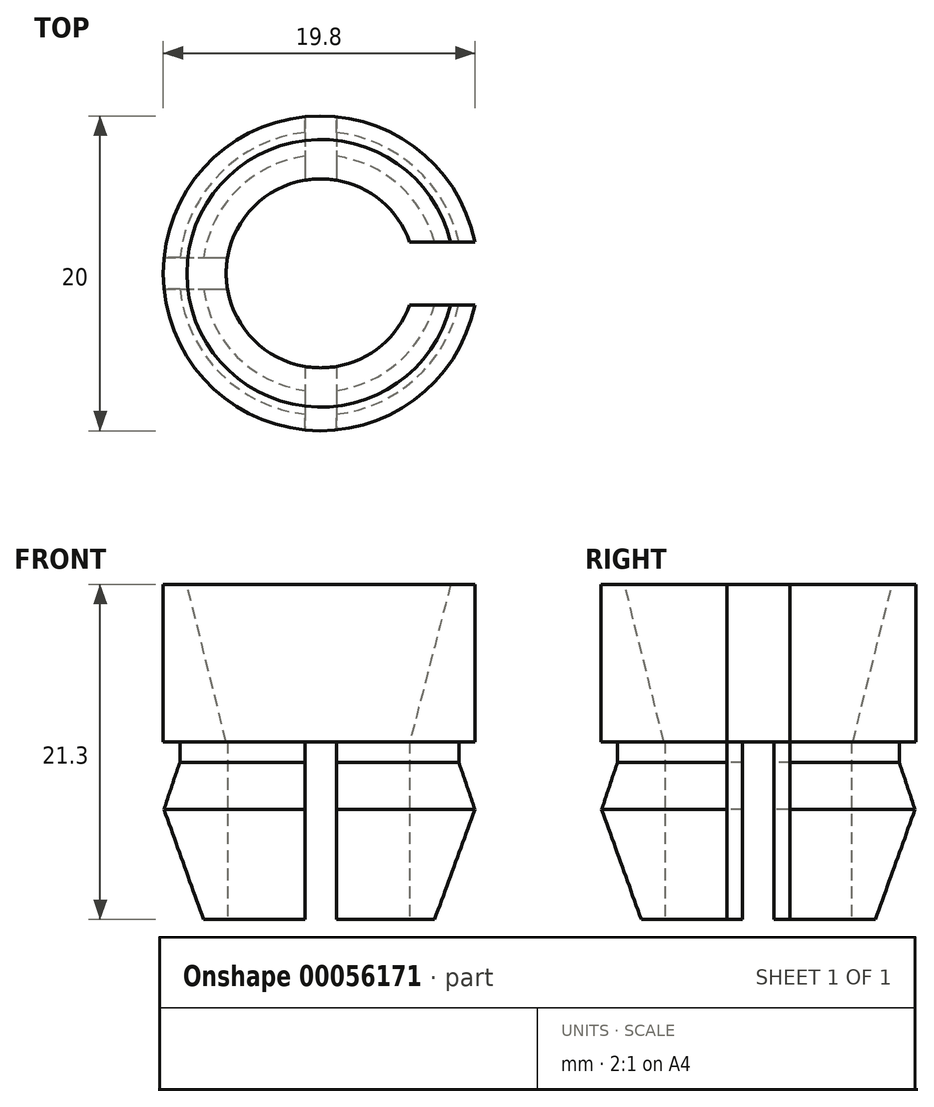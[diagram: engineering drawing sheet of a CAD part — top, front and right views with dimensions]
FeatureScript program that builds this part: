
annotation { "Feature Type Name" : "Feature", "Feature Type Description" : "" }
export const myFeature = defineFeature(function(context is Context, id is Id, definition is map)
    precondition{}
    {
        {
            var Q0;
            Q0=qCreatedBy(makeId("Top.planeOp"),FACE);
            var sketch = newSketch(context, id + "F0", { "sketchPlane" : qUnion([Q0])});
            skCircle(sketch, "E0", {"center": v(0, 0) * mm, "radius": 9 * mm});
            skSolve(sketch);
        }
        {
            var Q0;
            Q0=qCreatedBy(makeId("Front.planeOp"),FACE);
            var sketch = newSketch(context, id + "F1", { "sketchPlane" : qUnion([Q0])});
            skLineSegment(sketch, "E1", {"start": v(0, 0) * mm, "end": v(0, -3) * mm, "construction": true});
            skSolve(sketch);
        }
        {
            var Q0;
            Q0=makeQuery(id+"F0.imprint","IMPRINT",FACE,{"disambiguationData":[TD([[makeQuery(id+"F0.imprint","IMPRINT",EDGE,{"derivedFrom":sQuery(id+"F0.wireOp",EDGE,"E0")}),1.0]])]});
            var Q1;
            Q1=sQuery(id+"F1.wireOp",VERTEX,"E1.end");
            cPlane(context, id + "F2", {"entities" : qUnion([Q0, Q1]), "cplaneType" : CPlaneType.PLANE_POINT, "offset" : 1.3 * mm, "oppositeDirection" : true, "width" : 150 * mm, "height" : 150 * mm});
        }
        {
            var Q0;
            Q0=qCreatedBy(id+"F2.planeOp",FACE);
            var sketch = newSketch(context, id + "F3", { "sketchPlane" : qUnion([Q0])});
            skCircle(sketch, "E2", {"center": v(0, 0) * mm, "radius": 10 * mm});
            skSolve(sketch);
        }
        {
            var Q0;
            Q0=qCreatedBy(makeId("Front.planeOp"),FACE);
            var sketch = newSketch(context, id + "F4", { "sketchPlane" : qUnion([Q0])});
            skLineSegment(sketch, "E3", {"start": v(0, -10) * mm, "end": v(0, -3) * mm, "construction": true});
            skSolve(sketch);
        }
        {
            var Q0;
            Q0=makeQuery(id+"F3.imprint","IMPRINT",FACE,{"disambiguationData":[TD([[makeQuery(id+"F3.imprint","IMPRINT",EDGE,{"derivedFrom":sQuery(id+"F3.wireOp",EDGE,"E2")}),1.0]])]});
            var Q1;
            Q1=sQuery(id+"F4.wireOp",VERTEX,"E3.start");
            cPlane(context, id + "F5", {"entities" : qUnion([Q0, Q1]), "cplaneType" : CPlaneType.PLANE_POINT, "offset" : 5 * mm, "oppositeDirection" : true, "width" : 150 * mm, "height" : 150 * mm});
        }
        {
            var Q0;
            Q0=qCreatedBy(id+"F5.planeOp",FACE);
            var sketch = newSketch(context, id + "F6", { "sketchPlane" : qUnion([Q0])});
            skCircle(sketch, "E4", {"center": v(0, 0) * mm, "radius": 7.5 * mm});
            skSolve(sketch);
        }
        {
            var Q0;
            Q0=makeQuery(id+"F6.imprint","IMPRINT",FACE,{"disambiguationData":[TD([[makeQuery(id+"F6.imprint","IMPRINT",EDGE,{"derivedFrom":sQuery(id+"F6.wireOp",EDGE,"E4")}),1.0]])]});
            var Q1;
            Q1=makeQuery(id+"F3.imprint","IMPRINT",FACE,{"disambiguationData":[TD([[makeQuery(id+"F3.imprint","IMPRINT",EDGE,{"derivedFrom":sQuery(id+"F3.wireOp",EDGE,"E2")}),1.0]])]});
            loft(context, id + "F7", {"sheetProfilesArray" : [{ "sheetProfileEntities" : qUnion([Q0]) }, { "sheetProfileEntities" : qUnion([Q1]) }]});
        }
        {
            var Q1;
            Q1=makeQuery(id+"F0.imprint","IMPRINT",FACE,{"disambiguationData":[TD([[makeQuery(id+"F0.imprint","IMPRINT",EDGE,{"derivedFrom":sQuery(id+"F0.wireOp",EDGE,"E0")}),1.0]])]});
            var Q2;
            Q2=makeQuery(id+"F7.opLoft","CAP_FACE",FACE,{"disambiguationData":[OSD([makeQuery(id+"F3.imprint","IMPRINT",FACE,{"disambiguationData":[TD([[makeQuery(id+"F3.imprint","IMPRINT",EDGE,{"derivedFrom":sQuery(id+"F3.wireOp",EDGE,"E2")}),1.0]])]})])],"isStart":true});
            loft(context, id + "F8", {"operationType" : NewBodyOperationType.ADD, "sheetProfilesArray" : [{ "sheetProfileEntities" : qUnion([Q1]) }, { "sheetProfileEntities" : qUnion([Q2]) }]});
        }
        {
            var Q0;
            Q0=makeQuery(id+"F8.opLoft","CAP_FACE",FACE,{"disambiguationData":[OSD([makeQuery(id+"F0.imprint","IMPRINT",FACE,{"disambiguationData":[TD([[makeQuery(id+"F0.imprint","IMPRINT",EDGE,{"derivedFrom":sQuery(id+"F0.wireOp",EDGE,"E0")}),1.0]])]})])],"isStart":true});
            extrude(context, id + "F9", {"entities" : qUnion([Q0]), "operationType" : NewBodyOperationType.ADD, "depth" : 1.3 * mm});
        }
        {
            var Q0;
            {var subQ0=sQuery(id+"F6.wireOp",EDGE,"E4");var subQ1=sQuery(id+"F13.wireOp",EDGE,"E7.rect.top");var subQ4=sQuery(id+"F13.wireOp",EDGE,"E8.rect.right");var subQ5=makeQuery(id+"F13.imprint","INTERSECT",VERTEX,{"derivedFrom":[subQ1,subQ4]});Q0=makeQuery(id+"FMAczY7lawbJKEq_1.boolean.opBoolean","SPLIT",FACE,{"disambiguationData":[TD([makeQuery(id+"FMAczY7lawbJKEq_1.opExtrude","SWEPT_FACE",FACE,{"disambiguationData":[OSD([subQ1]),TDD([makeQuery(id+"F13.imprint","IMPRINT",EDGE,{"disambiguationData":[TD([[subQ5,-1.0]])],"derivedFrom":subQ1}),makeQuery(id+"F13.imprint","IMPRINT",EDGE,{"disambiguationData":[TD([[makeQuery(id+"F13.imprint","INTERSECT",VERTEX,{"derivedFrom":[subQ1,sQuery(id+"F13.wireOp",EDGE,"E7.rect.right")]}),1.0]])],"derivedFrom":subQ1})])]})])],"derivedFrom":makeQuery(id+"F7.opLoft","CAP_FACE",FACE,{"disambiguationData":[OSD([makeQuery(id+"F6.imprint","IMPRINT",FACE,{"disambiguationData":[TD([[makeQuery(id+"F6.imprint","IMPRINT",EDGE,{"derivedFrom":subQ0}),1.0]])]})])],"isStart":true})});}
            var sketch = newSketch(context, id + "F10", { "sketchPlane" : qUnion([Q0])});
            skCircle(sketch, "E5", {"center": v(0, 0) * mm, "radius": 6 * mm});
            skSolve(sketch);
        }
        {
            var Q0;
            Q0=makeQuery(id+"F9.opExtrude","CAP_FACE",FACE,{"disambiguationData":[OSD([makeQuery(id+"F0.imprint","IMPRINT",FACE,{"disambiguationData":[TD([[makeQuery(id+"F0.imprint","IMPRINT",EDGE,{"derivedFrom":sQuery(id+"F0.wireOp",EDGE,"E0")}),1.0]])]})])],"isStart":false});
            var sketch = newSketch(context, id + "F11", { "sketchPlane" : qUnion([Q0])});
            skCircle(sketch, "E6", {"center": v(0, 0) * mm, "radius": 10 * mm});
            skSolve(sketch);
        }
        {
            var Q0;
            Q0=makeQuery(id+"F11.imprint","IMPRINT",FACE,{"disambiguationData":[TD([[makeQuery(id+"F11.imprint","IMPRINT",EDGE,{"derivedFrom":sQuery(id+"F11.wireOp",EDGE,"E6")}),1.0]])]});
            var Q1;
            Q1=makeQuery(id+"F11.imprint","IMPRINT",FACE,{"disambiguationData":[TD([[makeQuery(id+"F11.imprint","IMPRINT",EDGE,{"derivedFrom":makeQuery(id+"F9.opExtrude","CAP_EDGE",EDGE,{"disambiguationData":[OSD([sQuery(id+"F0.wireOp",EDGE,"E0")])],"isStart":false})}),-1.0]])]});
            extrude(context, id + "F12", {"entities" : qUnion([Q0, Q1]), "operationType" : NewBodyOperationType.ADD, "depth" : 10 * mm});
        }
        {
            var Q0;
            Q0=makeQuery(id+"F7.opLoft","CAP_FACE",FACE,{"disambiguationData":[OSD([makeQuery(id+"F6.imprint","IMPRINT",FACE,{"disambiguationData":[TD([[makeQuery(id+"F6.imprint","IMPRINT",EDGE,{"derivedFrom":sQuery(id+"F6.wireOp",EDGE,"E4")}),1.0]])]})])],"isStart":true});
            var sketch = newSketch(context, id + "F13", { "sketchPlane" : qUnion([Q0])});
            skLineSegment(sketch, "E7.rect.bottom", {"start": v(-15, 1) * mm, "end": v(15, 1) * mm});
            skLineSegment(sketch, "E7.rect.top", {"start": v(-15, -1) * mm, "end": v(15, -1) * mm});
            skLineSegment(sketch, "E7.rect.left", {"start": v(-15, 1) * mm, "end": v(-15, -1) * mm});
            skLineSegment(sketch, "E7.rect.right", {"start": v(15, 1) * mm, "end": v(15, -1) * mm});
            skPoint(sketch, "E7.rect.middle", {"position": v(0, 0) * mm});
            skLineSegment(sketch, "E8.rect.bottom", {"start": v(-1, -15) * mm, "end": v(1, -15) * mm});
            skLineSegment(sketch, "E8.rect.top", {"start": v(-1, 15) * mm, "end": v(1, 15) * mm});
            skLineSegment(sketch, "E8.rect.left", {"start": v(-1, -15) * mm, "end": v(-1, 15) * mm});
            skLineSegment(sketch, "E8.rect.right", {"start": v(1, -15) * mm, "end": v(1, 15) * mm});
            skLineSegment(sketch, "E9", {"start": v(15, 1) * mm, "end": v(15, 2) * mm});
            skLineSegment(sketch, "E10", {"start": v(15, -1) * mm, "end": v(15, -2) * mm});
            skLineSegment(sketch, "E11", {"start": v(15, -2) * mm, "end": v(1, -2) * mm});
            skLineSegment(sketch, "E12", {"start": v(15, 2) * mm, "end": v(1, 2) * mm});
            skSolve(sketch);
        }
        {
            var Q0;
            Q0=makeQuery(id+"F10.imprint","IMPRINT",FACE,{"disambiguationData":[TD([[makeQuery(id+"F10.imprint","IMPRINT",EDGE,{"derivedFrom":sQuery(id+"F10.wireOp",EDGE,"E5")}),1.0]])]});
            var Q1;
            Q1=makeQuery(id+"F12.opExtrude","CAP_FACE",FACE,{"disambiguationData":[OSD([sQuery(id+"F11.wireOp",EDGE,"E6")])],"isStart":true});
            extrude(context, id + "F14", {"entities" : qUnion([Q0]), "operationType" : NewBodyOperationType.REMOVE, "endBound" : BoundingType.UP_TO_SURFACE, "oppositeDirection" : true, "endBoundEntityFace" : qUnion([Q1]), "depth" : 25 * mm});
        }
        {
            var Q0;
            Q0=makeQuery(id+"F12.opExtrude","CAP_FACE",FACE,{"disambiguationData":[OSD([sQuery(id+"F11.wireOp",EDGE,"E6")])],"isStart":false});
            var sketch = newSketch(context, id + "F15", { "sketchPlane" : qUnion([Q0])});
            skCircle(sketch, "E13", {"center": v(0, 0) * mm, "radius": 8.5 * mm});
            skSolve(sketch);
        }
        {
            var Q1;
            Q1=makeQuery(id+"F15.imprint","IMPRINT",FACE,{"disambiguationData":[TD([[makeQuery(id+"F15.imprint","IMPRINT",EDGE,{"derivedFrom":sQuery(id+"F15.wireOp",EDGE,"E13")}),1.0]])]});
            var Q2;
            Q2=makeQuery(id+"F14.boolean.opBoolean","COPY",FACE,{"derivedFrom":makeQuery(id+"F14.opExtrude","CAP_FACE",FACE,{"disambiguationData":[OSD([sQuery(id+"F10.wireOp",EDGE,"E5")])],"isStart":false})});
            loft(context, id + "F16", {"operationType" : NewBodyOperationType.REMOVE, "sheetProfilesArray" : [{ "sheetProfileEntities" : qUnion([Q1]) }, { "sheetProfileEntities" : qUnion([Q2]) }]});
        }
        {
            var Q0;
            {var subQ0=sQuery(id+"F13.wireOp",EDGE,"E8.rect.top");Q0=makeQuery(id+"F13.imprint","IMPRINT",FACE,{"disambiguationData":[TD([[makeQuery(id+"F13.imprint","IMPRINT",EDGE,{"derivedFrom":subQ0}),-1.0]])]});}
            var Q1;
            {var subQ0=sQuery(id+"F13.wireOp",EDGE,"E8.rect.left");var subQ1=sQuery(id+"F13.wireOp",EDGE,"E7.rect.bottom");var subQ2=makeQuery(id+"F13.imprint","INTERSECT",VERTEX,{"derivedFrom":[subQ1,subQ0]});Q1=makeQuery(id+"F13.imprint","IMPRINT",FACE,{"disambiguationData":[TD([[makeQuery(id+"F13.imprint","IMPRINT",EDGE,{"disambiguationData":[TD([[subQ2,-1.0]])],"derivedFrom":subQ1}),1.0]])]});}
            var Q2;
            {var subQ0=sQuery(id+"F13.wireOp",EDGE,"E7.rect.right");Q2=makeQuery(id+"F13.imprint","IMPRINT",FACE,{"disambiguationData":[TD([[makeQuery(id+"F13.imprint","IMPRINT",EDGE,{"derivedFrom":subQ0}),-1.0]])]});}
            var Q3;
            {var subQ0=sQuery(id+"F13.wireOp",EDGE,"E8.rect.right");var subQ1=sQuery(id+"F13.wireOp",EDGE,"E7.rect.bottom");var subQ2=makeQuery(id+"F13.imprint","INTERSECT",VERTEX,{"derivedFrom":[subQ1,subQ0]});Q3=makeQuery(id+"F13.imprint","IMPRINT",FACE,{"disambiguationData":[TD([[makeQuery(id+"F13.imprint","IMPRINT",EDGE,{"disambiguationData":[TD([[subQ2,-1.0]])],"derivedFrom":subQ1}),-1.0]])]});}
            var Q4;
            {var subQ0=sQuery(id+"F13.wireOp",EDGE,"E7.rect.left");Q4=makeQuery(id+"F13.imprint","IMPRINT",FACE,{"disambiguationData":[TD([[makeQuery(id+"F13.imprint","IMPRINT",EDGE,{"derivedFrom":subQ0}),1.0]])]});}
            var Q5;
            {var subQ0=sQuery(id+"F13.wireOp",EDGE,"E8.rect.left");var subQ1=sQuery(id+"F13.wireOp",EDGE,"E7.rect.bottom");var subQ2=makeQuery(id+"F13.imprint","INTERSECT",VERTEX,{"derivedFrom":[subQ1,subQ0]});Q5=makeQuery(id+"F13.imprint","IMPRINT",FACE,{"disambiguationData":[TD([[makeQuery(id+"F13.imprint","IMPRINT",EDGE,{"disambiguationData":[TD([[subQ2,1.0]])],"derivedFrom":subQ1}),-1.0]])]});}
            var Q6;
            {var subQ0=sQuery(id+"F13.wireOp",EDGE,"E8.rect.left");var subQ1=sQuery(id+"F13.wireOp",EDGE,"E7.rect.bottom");var subQ2=makeQuery(id+"F13.imprint","INTERSECT",VERTEX,{"derivedFrom":[subQ1,subQ0]});Q6=makeQuery(id+"F13.imprint","IMPRINT",FACE,{"disambiguationData":[TD([[makeQuery(id+"F13.imprint","IMPRINT",EDGE,{"disambiguationData":[TD([[subQ2,-1.0]])],"derivedFrom":subQ1}),-1.0]])]});}
            var Q7;
            {var subQ0=sQuery(id+"F13.wireOp",EDGE,"E8.rect.left");var subQ1=sQuery(id+"F13.wireOp",EDGE,"E7.rect.top");var subQ2=makeQuery(id+"F13.imprint","INTERSECT",VERTEX,{"derivedFrom":[subQ1,subQ0]});Q7=makeQuery(id+"F13.imprint","IMPRINT",FACE,{"disambiguationData":[TD([[makeQuery(id+"F13.imprint","IMPRINT",EDGE,{"disambiguationData":[TD([[subQ2,-1.0]])],"derivedFrom":subQ1}),-1.0]])]});}
            var Q8;
            {var subQ0=sQuery(id+"F13.wireOp",EDGE,"E8.rect.bottom");Q8=makeQuery(id+"F13.imprint","IMPRINT",FACE,{"disambiguationData":[TD([[makeQuery(id+"F13.imprint","IMPRINT",EDGE,{"derivedFrom":subQ0}),1.0]])]});}
            var Q9;
            Q9=makeQuery(id+"F12.opExtrude","CAP_FACE",FACE,{"disambiguationData":[OSD([sQuery(id+"F11.wireOp",EDGE,"E6")])],"isStart":true});
            extrude(context, id + "F17", {"entities" : qUnion([Q0, Q1, Q2, Q3, Q4, Q5, Q6, Q7, Q8]), "operationType" : NewBodyOperationType.REMOVE, "endBound" : BoundingType.UP_TO_SURFACE, "oppositeDirection" : true, "endBoundEntityFace" : qUnion([Q9]), "depth" : 25 * mm});
        }
        {
            var Q0;
            {var subQ0=sQuery(id+"F13.wireOp",EDGE,"E8.rect.right");var subQ1=sQuery(id+"F13.wireOp",EDGE,"E7.rect.top");var subQ2=makeQuery(id+"F13.imprint","INTERSECT",VERTEX,{"derivedFrom":[subQ1,subQ0]});Q0=makeQuery(id+"F13.imprint","IMPRINT",FACE,{"disambiguationData":[TD([[makeQuery(id+"F13.imprint","IMPRINT",EDGE,{"disambiguationData":[TD([[subQ2,-1.0]])],"derivedFrom":subQ1}),-1.0]])]});}
            var Q1;
            {var subQ0=sQuery(id+"F13.wireOp",EDGE,"E8.rect.right");var subQ1=sQuery(id+"F13.wireOp",EDGE,"E7.rect.bottom");var subQ2=makeQuery(id+"F13.imprint","INTERSECT",VERTEX,{"derivedFrom":[subQ1,subQ0]});Q1=makeQuery(id+"F13.imprint","IMPRINT",FACE,{"disambiguationData":[TD([[makeQuery(id+"F13.imprint","IMPRINT",EDGE,{"disambiguationData":[TD([[subQ2,-1.0]])],"derivedFrom":subQ1}),-1.0]])]});}
            var Q2;
            {var subQ0=sQuery(id+"F13.wireOp",EDGE,"E8.rect.right");var subQ1=sQuery(id+"F13.wireOp",EDGE,"E7.rect.bottom");var subQ2=makeQuery(id+"F13.imprint","INTERSECT",VERTEX,{"derivedFrom":[subQ1,subQ0]});Q2=makeQuery(id+"F13.imprint","IMPRINT",FACE,{"disambiguationData":[TD([[makeQuery(id+"F13.imprint","IMPRINT",EDGE,{"disambiguationData":[TD([[subQ2,-1.0]])],"derivedFrom":subQ1}),1.0]])]});}
            var Q3;
            {var subQ0=sQuery(id+"F13.wireOp",EDGE,"E9");Q3=makeQuery(id+"F13.imprint","IMPRINT",FACE,{"disambiguationData":[TD([[makeQuery(id+"F13.imprint","IMPRINT",EDGE,{"derivedFrom":subQ0}),1.0]])]});}
            var Q4;
            {var subQ0=sQuery(id+"F13.wireOp",EDGE,"E7.rect.right");Q4=makeQuery(id+"F13.imprint","IMPRINT",FACE,{"disambiguationData":[TD([[makeQuery(id+"F13.imprint","IMPRINT",EDGE,{"derivedFrom":subQ0}),-1.0]])]});}
            var Q5;
            {var subQ0=sQuery(id+"F13.wireOp",EDGE,"E10");Q5=makeQuery(id+"F13.imprint","IMPRINT",FACE,{"disambiguationData":[TD([[makeQuery(id+"F13.imprint","IMPRINT",EDGE,{"derivedFrom":subQ0}),-1.0]])]});}
            extrude(context, id + "F18", {"entities" : qUnion([Q0, Q1, Q2, Q3, Q4, Q5]), "operationType" : NewBodyOperationType.REMOVE, "endBound" : BoundingType.THROUGH_ALL, "oppositeDirection" : true, "depth" : 25 * mm});
        }
    });
